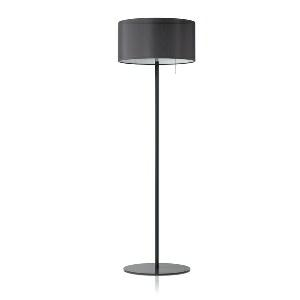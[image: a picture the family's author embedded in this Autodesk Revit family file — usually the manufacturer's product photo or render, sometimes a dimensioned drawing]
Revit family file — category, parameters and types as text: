
# Revit family: vivaa_free_-_vfs_7000_vtl_d_00812677_3c6c
name_source: partatom
category: Lighting Fixtures
units: mm (PartAtom-declared; Revit-internal decimal feet)

## family parameters
Cut with Voids When Loaded = No
Host = Face
Light Source = No
Part Type = Normal
Room Calculation Point = No
Round Connector Dimension = Use Diameter
Shared = No

## types (1)
- VIVAA.free - VFS 7000/VTL/D (1 x LED, 7200 lm, 2700-6500K)
    Apparent Load = 79 VA
    Approval mark = CE
    CIE Flux Codes = 52 82 95 44 100
    Color Rendering = 90-100
    Color Temperature = 2700-6500K
    Control Gear = Electronic ballast
    Default Elevation = 1800 mm
    Description = VFS 7000/VTL/D|Free-standing luminaire|light source:   Daylight   |work equipment: Electronic ballast|luminous flux: 7200 lm|light distribution: Direct/indirect|direct ratio: approx. 44 %|color rendering index (CRI): >= 90|chromaticity tolerance:  3 SDCM|technology: Continuously dimmable|operation: Pull cord|luminaire body|material: Polyethylene(PE)|surface: Untreated|colour: Anthracite|lamp cover: Polycarbonate (PC), Satine|tubular section|material: Steel tube|surface: Painted|Form: Tubular section upright|colour of tubular section: Anthracite grey|luminaire base|Form: Round (flat)|weight (net): approx. 12.3 kg|mains lead: 2.20 m Mains plug CEE 7/VII|Fastening: Floor standing base|glare control: Diffusor|luminance(L65): <= 1600 cd/m|unified glare rating(4H 8H): <=  16|special features: App control, Biodynamic light VTL|
    Frequency = 50 Hz, 60 Hz
    Height = 250 mm
    Lamp = 1 x LED
    Lamp Light Flux = 7200 lm
    Lamp count = 1
    Length = 520 mm
    Luminous efficacy = 91 lm/W
    Manufacturer = Waldmann
    ModVariant = No
    Model = 00812677
    Mounting Place = Floor
    Mounting Type = Freestanding
    Number of Poles = 1
    OnlyDefault = Yes
    Power Factor = 1
    Product Name = VIVAA.free - VFS 7000/VTL/D
    Product group = Free standing luminaire
    ProductGroupID = 13
    Protection Class = Protection class I
    Protection Degree = Degree of protection
    RLX_Detail_Level = 1
    RLX_Emergency_Light_Flux = 0 lm
    RLX_Emergency_Type = 0
    RLX_Emergency_Type_DB = No
    RlxData = <blob elided: 19337 chars, md5=bcef1355>
    Socket = socket
    Standby Power = 0 W
    System Light Flux = 7200 lm
    System Power = 79 W
    Type Comments = Product without accessories
    Type Image = vivaa_free_metal_sw.jpg
    URL = http://relux.com
    VarID = ---
    Voltage = 230 V
    Voltage Range = 220-240 V
    Weight = 0.00 kg
    Width = 0 mm  [stored 0 ft]

note: [stored X ft] marks values corroborated as IEEE doubles in the binary element streams (Revit-internal decimal feet)

## geometry (parser evidence)
native form markers: Blend x4, Sweep x15
no freeform markers — native parametric forms only
